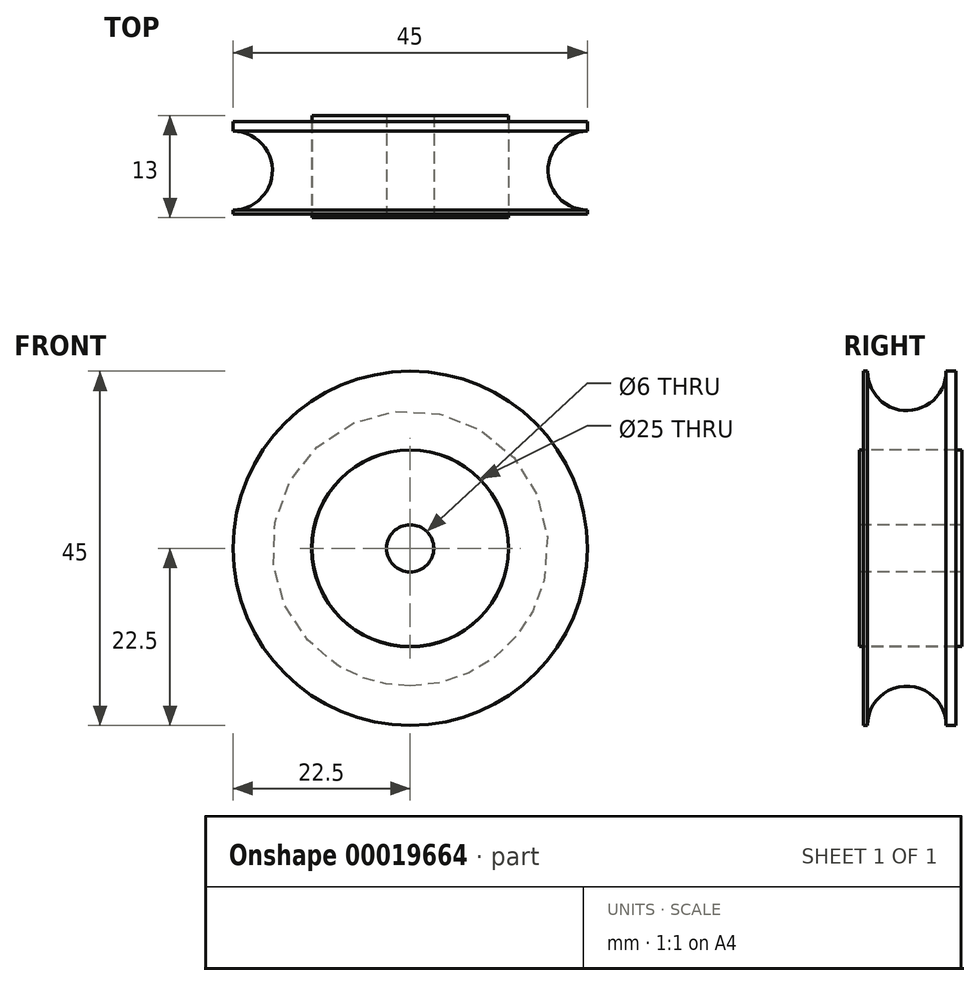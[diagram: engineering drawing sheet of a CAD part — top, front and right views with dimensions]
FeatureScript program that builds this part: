
annotation { "Feature Type Name" : "Feature", "Feature Type Description" : "" }
export const myFeature = defineFeature(function(context is Context, id is Id, definition is map)
    precondition{}
    {
        {
            var Q0;
            Q0=qCreatedBy(makeId("Top.planeOp"),FACE);
            var sketch = newSketch(context, id + "F0", { "sketchPlane" : qUnion([Q0])});
            skLineSegment(sketch, "E0", {"start": v(22.5, 0) * mm, "end": v(45, 0) * mm});
            skLineSegment(sketch, "E1", {"start": v(45, 0) * mm, "end": v(45, 1) * mm});
            skArc(sketch, "E2", {"start": v(45, 11) * mm, "mid": v(40, 6) * mm, "end": v(45, 1) * mm});
            skLineSegment(sketch, "E3", {"start": v(45, 11) * mm, "end": v(45, 12.23) * mm});
            skLineSegment(sketch, "E4", {"start": v(45, 12.23) * mm, "end": v(22.5, 12.23) * mm});
            skLineSegment(sketch, "E5", {"start": v(22.5, 0) * mm, "end": v(22.5, 12.23) * mm});
            skPoint(sketch, "E6.orphan", {"position": v(0, 12.23) * mm});
            skPoint(sketch, "E7.orphan", {"position": v(0, 0) * mm});
            skSolve(sketch);
        }
        {
            var Q0;
            Q0=makeQuery(id+"F0.imprint","IMPRINT",FACE,{"disambiguationData":[TD([[makeQuery(id+"F0.imprint","IMPRINT",EDGE,{"derivedFrom":sQuery(id+"F0.wireOp",EDGE,"E0")}),1.0]])]});
            var Q1;
            Q1=sQuery(id+"F0.wireOp",EDGE,"E5");
            revolve(context, id + "F1", {"entities" : qUnion([Q0]), "axis" : qUnion([Q1]), "revolveType" : RevolveType.FULL});
        }
        {
            var Q0;
            Q0=makeQuery(id+"F1.opRevolve","SWEPT_FACE",FACE,{"disambiguationData":[OSD([sQuery(id+"F0.wireOp",EDGE,"E0")])]});
            var sketch = newSketch(context, id + "F2", { "sketchPlane" : qUnion([Q0])});
            skCircle(sketch, "E8", {"center": v(22.5, 0) * mm, "radius": 3 * mm});
            skSolve(sketch);
        }
        {
            var Q0;
            Q0=makeQuery(id+"F2.imprint","IMPRINT",FACE,{"disambiguationData":[TD([[makeQuery(id+"F2.imprint","IMPRINT",EDGE,{"derivedFrom":sQuery(id+"F2.wireOp",EDGE,"E8")}),1.0]])]});
            extrude(context, id + "F3", {"entities" : qUnion([Q0]), "operationType" : NewBodyOperationType.REMOVE, "oppositeDirection" : true, "depth" : 25 * mm});
        }
        {
            var Q0;
            Q0=qCreatedBy(makeId("Front.planeOp"),FACE);
            var sketch = newSketch(context, id + "F4", { "sketchPlane" : qUnion([Q0])});
            skCircle(sketch, "E9.0", {"center": v(22.5, 0) * mm, "radius": 12.5 * mm});
            skSolve(sketch);
        }
        {
            var Q0;
            Q0=makeQuery(id+"F4.imprint","IMPRINT",FACE,{"disambiguationData":[TD([[makeQuery(id+"F4.imprint","IMPRINT",EDGE,{"derivedFrom":sQuery(id+"F4.wireOp",EDGE,"E9.0")}),1.0]])]});
            extrude(context, id + "F5", {"entities" : qUnion([Q0]), "operationType" : NewBodyOperationType.REMOVE, "oppositeDirection" : true, "depth" : 13 * mm});
        }
        {
            var Q0;
            Q0=qCreatedBy(makeId("Front.planeOp"),FACE);
            var sketch = newSketch(context, id + "F6", { "sketchPlane" : qUnion([Q0])});
            skCircle(sketch, "E10.0", {"center": v(22.5, 0) * mm, "radius": 12.47 * mm});
            skCircle(sketch, "E11.0", {"center": v(22.5, 0) * mm, "radius": 3 * mm});
            skSolve(sketch);
        }
        {
            var Q0;
            Q0=makeQuery(id+"F6.imprint","IMPRINT",FACE,{"disambiguationData":[TD([[makeQuery(id+"F6.imprint","IMPRINT",EDGE,{"derivedFrom":sQuery(id+"F6.wireOp",EDGE,"E10.0")}),1.0]])]});
            extrude(context, id + "F7", {"entities" : qUnion([Q0]), "oppositeDirection" : true, "depth" : 13 * mm});
        }
        {
            var Q0;
            Q0=makeQuery(id+"F1.opRevolve","SWEPT_FACE",FACE,{"disambiguationData":[OSD([sQuery(id+"F0.wireOp",EDGE,"E0")])]});
            extrude(context, id + "F8", {"entities" : qUnion([Q0]), "operationType" : NewBodyOperationType.REMOVE, "oppositeDirection" : true, "depth" : .5 * mm});
        }
        {
            var Q0;
            Q0=makeQuery(id+"F1.opRevolve","SWEPT_FACE",FACE,{"disambiguationData":[OSD([sQuery(id+"F0.wireOp",EDGE,"E4")])]});
            extrude(context, id + "F9", {"entities" : qUnion([Q0]), "operationType" : NewBodyOperationType.ADD, "oppositeDirection" : true, "depth" : .5 * mm});
        }
    });
